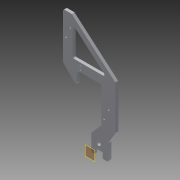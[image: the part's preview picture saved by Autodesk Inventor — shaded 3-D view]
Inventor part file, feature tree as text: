
AUTODESK INVENTOR PART (.ipt)
format: ipt  version: 2013 (Build 170138000, 138)  size: 190,464 bytes
history: native  units: in
note: dims shown in document units (in); Inventor stores cm internally (conversion verified against a paired STEP export)
features: sketch x4, extrude x4, plane x2, fillet x1
ambient origin geometry x8: Origin, YZ Plane, XZ Plane, XY Plane, X Axis, Y Axis, Z Axis, Center Point
bodies: Solid1 (feature_tree)
feature tree (11):
  sketch  "Sketch1"  dims[d0=0.25in d1=0.5in d2=0.75in d3=0.25in d5=0.3765in d6=0.5in d7=0.375in d11=1.25in d23=1.0in]
  plane  "Work Plane1"
  plane  "Work Plane2"
  extrude  "Extrusion6"  Depth=1.0in
  extrude  "Extrusion7"  Depth=1.0in
  fillet  "Fillet3"  Radius=1.5in
  extrude  "Extrusion8"  Depth=0.25in
  extrude  "Extrusion9"  Depth=1.5in
  sketch  "Sketch5"  dims[d24=1.5in d25=1.0in d26=1.5in]
  sketch  "Sketch6"  dims[d27=2.15in d32=0.25in]
  sketch  "Sketch7"  dims[d33=0.875in d34=1.5in d36=3.125in d59=4.8333in d60=4.625in d61=4.0833in d62=0.75in d64=1.25in d66=1.225in d88=0.5in d89=0.2797in d91=0.85in d92=0.75in d93=0.25in d94=0.0in d95=0.15in d96=0.15in d97=1.113in d98=2.019in d99=0.2375in d100=0.6355in d101=0.375in d102=0.0in d103=0.125in d104=0.125in d105=0.125in d106=0.1875in d107=0.25in d108=0.375in d109=0.0in d110=1.5in d111=1.5in d112=1.5in d113=0.15in d114=0.15in d115=0.906in d116=0.398in d117=0.237in d118=0.125in d119=0.375in d120=0.0in]
